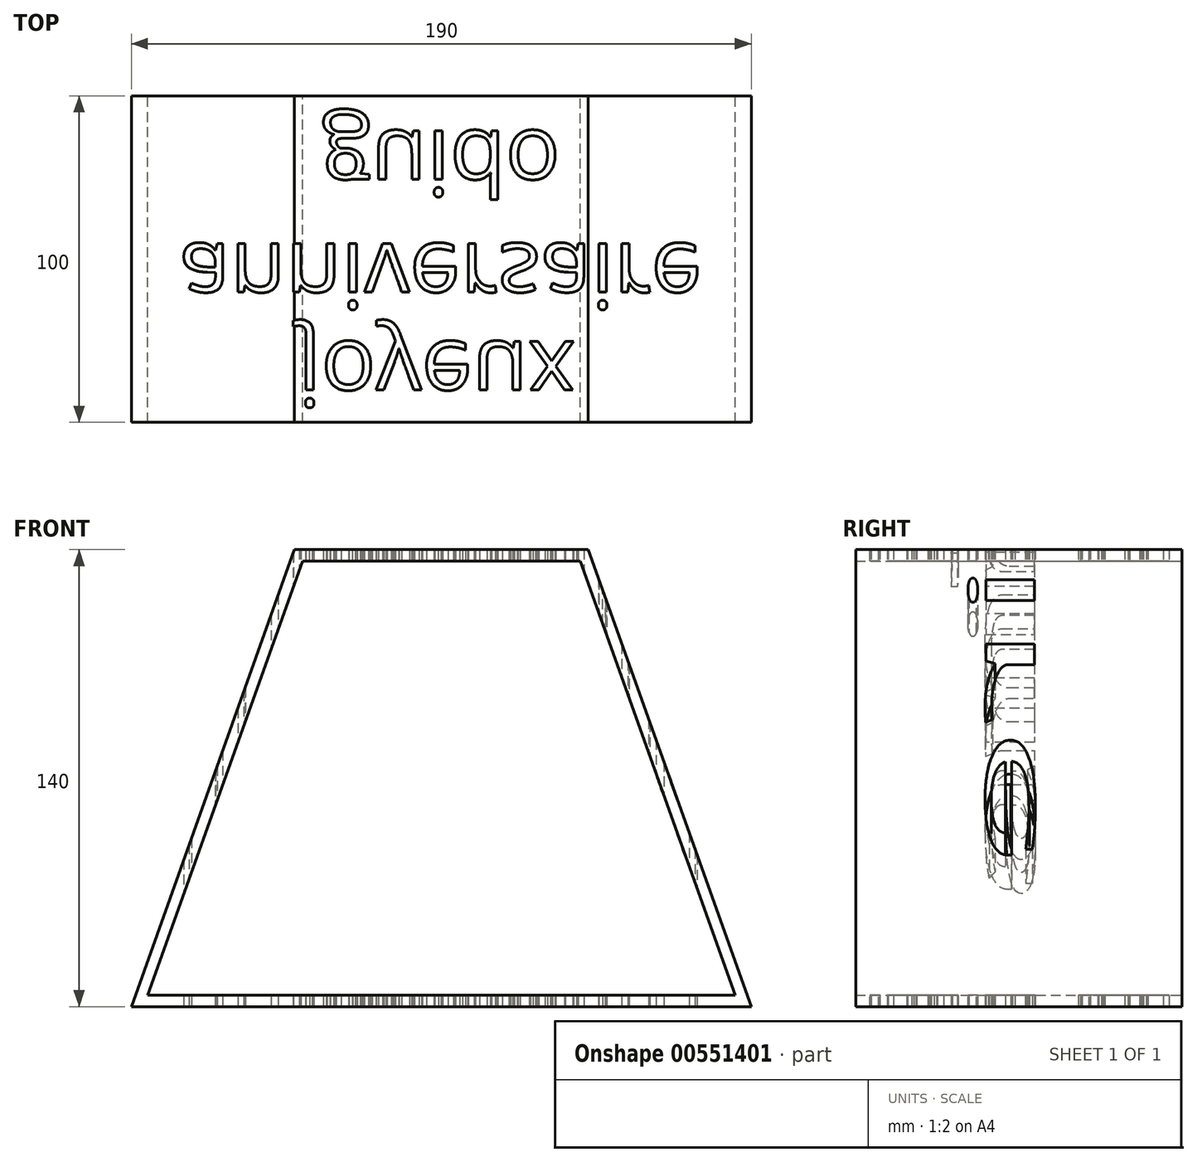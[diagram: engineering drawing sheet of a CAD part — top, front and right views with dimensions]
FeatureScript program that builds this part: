
annotation { "Feature Type Name" : "Feature", "Feature Type Description" : "" }
export const myFeature = defineFeature(function(context is Context, id is Id, definition is map)
    precondition{}
    {
        {
            var Q0;
            Q0=qCreatedBy(makeId("Front.planeOp"),FACE);
            var sketch = newSketch(context, id + "F0", { "sketchPlane" : qUnion([Q0])});
            skLineSegment(sketch, "E0", {"start": v(95, 0) * mm, "end": v(-95, 0) * mm});
            skLineSegment(sketch, "E1", {"start": v(45, 140) * mm, "end": v(-45, 140) * mm});
            skLineSegment(sketch, "E2", {"start": v(0, 0) * mm, "end": v(0, 140) * mm, "construction": true});
            skLineSegment(sketch, "E3", {"start": v(95, 0) * mm, "end": v(45, 140) * mm});
            skLineSegment(sketch, "E4", {"start": v(-45, 140) * mm, "end": v(-95, 0) * mm});
            skSolve(sketch);
        }
        {
            var Q0;
            Q0=makeQuery(id+"F0.imprint","IMPRINT",FACE,{"disambiguationData":[TD([[makeQuery(id+"F0.imprint","IMPRINT",EDGE,{"derivedFrom":sQuery(id+"F0.wireOp",EDGE,"E0")}),-1.0]])]});
            extrude(context, id + "F1", {"entities" : qUnion([Q0]), "depth" : 100 * mm, "offsetDistance" : 25 * mm});
        }
        {
            var Q0;
            Q0=makeQuery(id+"F1.opExtrude","CAP_FACE",FACE,{"disambiguationData":[OSD([sQuery(id+"F0.wireOp",EDGE,"E0"),sQuery(id+"F0.wireOp",EDGE,"E1"),sQuery(id+"F0.wireOp",EDGE,"E3"),sQuery(id+"F0.wireOp",EDGE,"E4")])],"isStart":false});
            var Q1;
            Q1=makeQuery(id+"F1.opExtrude","CAP_FACE",FACE,{"disambiguationData":[OSD([sQuery(id+"F0.wireOp",EDGE,"E0"),sQuery(id+"F0.wireOp",EDGE,"E1"),sQuery(id+"F0.wireOp",EDGE,"E3"),sQuery(id+"F0.wireOp",EDGE,"E4")])],"isStart":true});
            shell(context, id + "F2", {"entities" : qUnion([Q0, Q1]), "thickness" : 3.5 * mm});
        }
        {
            var Q0;
            Q0=makeQuery(id+"F1.opExtrude","SWEPT_FACE",FACE,{"disambiguationData":[OSD([sQuery(id+"F0.wireOp",EDGE,"E0")])]});
            var sketch = newSketch(context, id + "F3", { "sketchPlane" : qUnion([Q0])});
            skText(sketch, "E5", { "text": "joyeux", "fontName": "OpenSans-Regular.ttf"});
            const initialGuessF3  = {"E5": [-0.04387, 0.07521, 1, 0, 0.02]};
            skSetInitialGuess(sketch, initialGuessF3);
            skSolve(sketch);
        }
        {
            var Q0;
            Q0=makeQuery(id+"F3.imprint","IMPRINT",FACE,{"disambiguationData":[TD([[makeQuery(id+"F3.imprint","IMPRINT",EDGE,{"derivedFrom":sQuery(id+"F3.wireOp",EDGE,"E5.sketch_text.stroke-0")}),1.0]])]});
            var sketch = newSketch(context, id + "F4", { "sketchPlane" : qUnion([Q0])});
            skText(sketch, "E6", { "text": "anniversaire\n", "fontName": "OpenSans-Regular.ttf"});
            const initialGuessF4  = {"E6": [-0.0802, 0.04521, 1, 0, 0.02]};
            skSetInitialGuess(sketch, initialGuessF4);
            skSolve(sketch);
        }
        {
            var Q0;
            Q0=makeQuery(id+"F3.imprint","IMPRINT",FACE,{"disambiguationData":[TD([[makeQuery(id+"F3.imprint","IMPRINT",EDGE,{"derivedFrom":sQuery(id+"F3.wireOp",EDGE,"E5.sketch_text.stroke-0")}),1.0]])]});
            var sketch = newSketch(context, id + "F5", { "sketchPlane" : qUnion([Q0])});
            skText(sketch, "E7", { "text": "guido", "fontName": "OpenSans-Regular.ttf"});
            const initialGuessF5  = {"E7": [-0.03667, 0.01064, 1, 0, 0.02]};
            skSetInitialGuess(sketch, initialGuessF5);
            skSolve(sketch);
        }
        {
            var Q0;
            Q0 = qSketchRegion(id + "F3", true);
            var Q1;
            Q1 = qSketchRegion(id + "F4", true);
            var Q2;
            Q2 = qSketchRegion(id + "F5", true);
            extrude(context, id + "F6", {"entities" : qUnion([Q0, Q1, Q2]), "operationType" : NewBodyOperationType.REMOVE, "endBound" : BoundingType.THROUGH_ALL, "oppositeDirection" : true, "depth" : 25 * mm, "offsetDistance" : 25 * mm});
        }
    });
